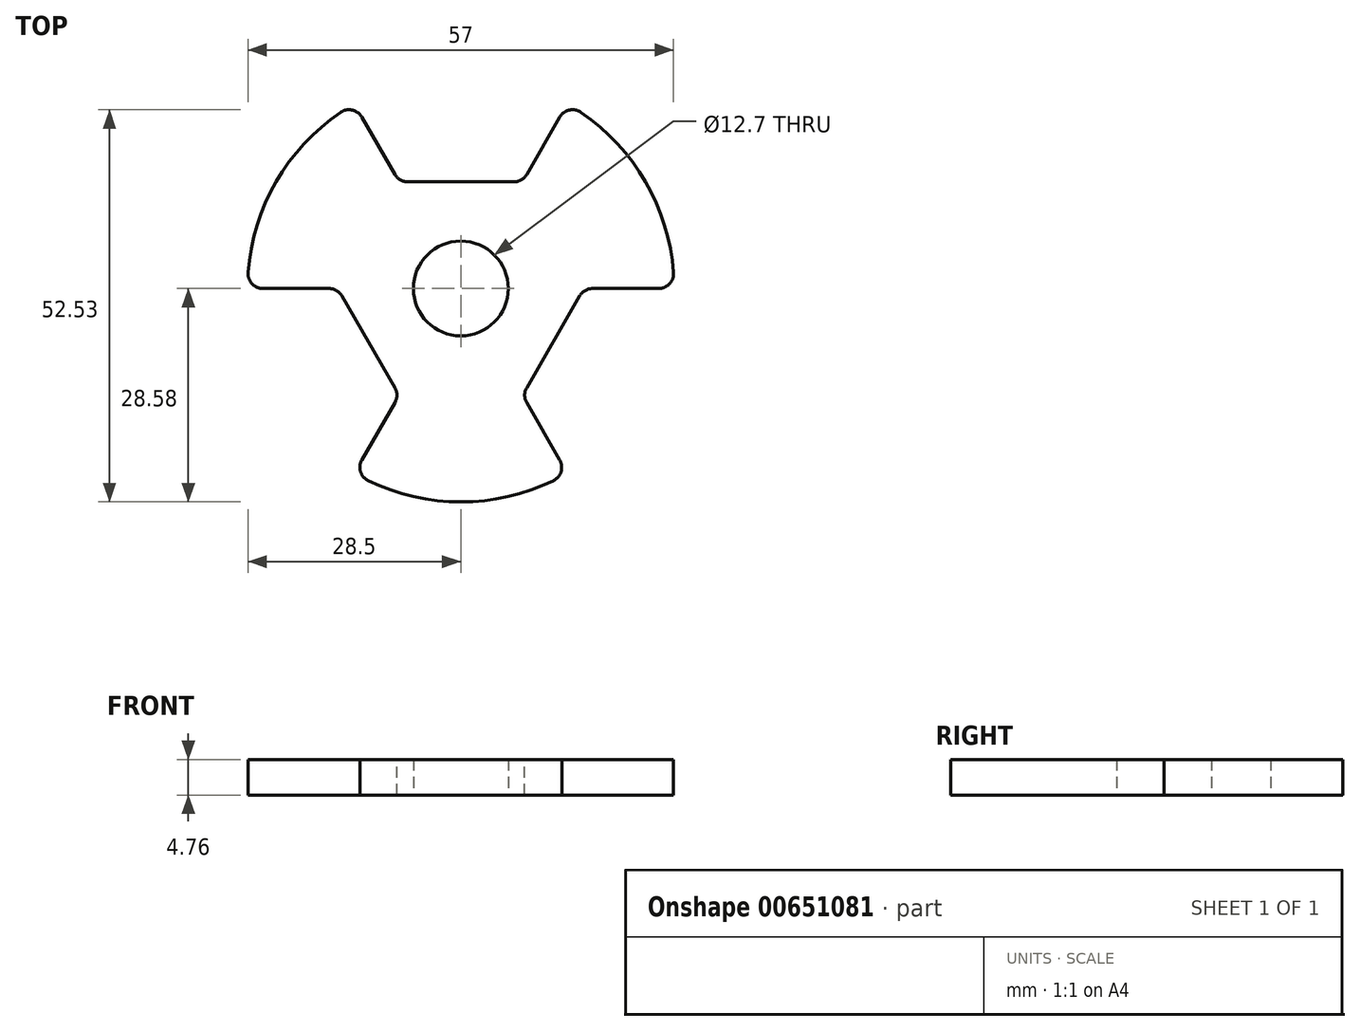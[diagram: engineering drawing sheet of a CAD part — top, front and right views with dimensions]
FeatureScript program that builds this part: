
annotation { "Feature Type Name" : "Feature", "Feature Type Description" : "" }
export const myFeature = defineFeature(function(context is Context, id is Id, definition is map)
    precondition{}
    {
        {
            var Q0;
            Q0=qCreatedBy(makeId("Top.planeOp"),FACE);
            var sketch = newSketch(context, id + "F0", { "sketchPlane" : qUnion([Q0])});
            skCircle(sketch, "E0", {"center": v(0, 0) * mm, "radius": 6.35 * mm});
            skCircle(sketch, "E1", {"center": v(0, 0) * mm, "radius": 28.58 * mm});
            skLineSegment(sketch, "E2", {"start": v(0, 0) * mm, "end": v(0, 28.58) * mm});
            skLineSegment(sketch, "E3", {"start": v(0, 0) * mm, "end": v(24.75, -14.29) * mm});
            skLineSegment(sketch, "E4", {"start": v(0, 0) * mm, "end": v(-24.75, -14.29) * mm});
            skLineSegment(sketch, "E5", {"start": v(0, 28.58) * mm, "end": v(-24.75, -14.29) * mm});
            skLineSegment(sketch, "E6", {"start": v(-24.75, -14.29) * mm, "end": v(24.75, -14.29) * mm});
            skLineSegment(sketch, "E7", {"start": v(24.75, -14.29) * mm, "end": v(0, 28.58) * mm});
            skLineSegment(sketch, "E8", {"start": v(0, 0) * mm, "end": v(0, -28.58) * mm});
            skPoint(sketch, "E8.endSnap0", {"position": v(0, -14.29) * mm});
            skLineSegment(sketch, "E9", {"start": v(0, 0) * mm, "end": v(24.75, 14.29) * mm});
            skLineSegment(sketch, "E10", {"start": v(0, 0) * mm, "end": v(-24.75, 14.29) * mm});
            skLineSegment(sketch, "E11", {"start": v(-24.75, 14.29) * mm, "end": v(0, -28.58) * mm});
            skLineSegment(sketch, "E12", {"start": v(24.75, 14.29) * mm, "end": v(0, -28.58) * mm});
            skLineSegment(sketch, "E13", {"start": v(-24.75, 14.29) * mm, "end": v(24.75, 14.29) * mm});
            skLineSegment(sketch, "E14", {"start": v(0, 0) * mm, "end": v(28.58, 0) * mm});
            skLineSegment(sketch, "E15", {"start": v(0, 0) * mm, "end": v(-14.29, -24.75) * mm});
            skLineSegment(sketch, "E16", {"start": v(0, 0) * mm, "end": v(-14.29, 24.75) * mm});
            skLineSegment(sketch, "E17", {"start": v(-14.29, 24.75) * mm, "end": v(-14.29, -24.75) * mm});
            skLineSegment(sketch, "E18", {"start": v(-14.29, -24.75) * mm, "end": v(28.58, 0) * mm});
            skLineSegment(sketch, "E19", {"start": v(28.58, 0) * mm, "end": v(-14.29, 24.75) * mm});
            skLineSegment(sketch, "E20", {"start": v(0, 0) * mm, "end": v(-28.58, 0) * mm});
            skLineSegment(sketch, "E21", {"start": v(0, 0) * mm, "end": v(14.29, -24.75) * mm});
            skLineSegment(sketch, "E22", {"start": v(0, 0) * mm, "end": v(14.29, 24.75) * mm});
            skLineSegment(sketch, "E23", {"start": v(14.29, 24.75) * mm, "end": v(-28.58, 0) * mm});
            skLineSegment(sketch, "E24", {"start": v(14.29, -24.75) * mm, "end": v(-28.58, 0) * mm});
            skLineSegment(sketch, "E25", {"start": v(14.29, 24.75) * mm, "end": v(14.29, -24.75) * mm});
            skCircle(sketch, "E26", {"center": v(0, 0) * mm, "radius": 5.08 * mm});
            skSolve(sketch);
        }
        {
            var Q0;
            {var subQ1=sQuery(id+"F0.wireOp",EDGE,"E0");var subQ7=sQuery(id+"F0.wireOp",EDGE,"E4");var subQ9=makeQuery(id+"F0.imprint","INTERSECT",VERTEX,{"derivedFrom":[subQ1,subQ7]});Q0=makeQuery(id+"F0.imprint","IMPRINT",FACE,{"disambiguationData":[TD([[makeQuery(id+"F0.imprint","IMPRINT",EDGE,{"disambiguationData":[TD([[subQ9,-1.0]])],"derivedFrom":subQ1}),-1.0]])]});}
            var Q1;
            {var subQ5=sQuery(id+"F0.wireOp",EDGE,"E0");var subQ7=sQuery(id+"F0.wireOp",EDGE,"E21");var subQ9=makeQuery(id+"F0.imprint","INTERSECT",VERTEX,{"derivedFrom":[subQ5,subQ7]});Q1=makeQuery(id+"F0.imprint","IMPRINT",FACE,{"disambiguationData":[TD([[makeQuery(id+"F0.imprint","IMPRINT",EDGE,{"disambiguationData":[TD([[subQ9,-1.0]])],"derivedFrom":subQ5}),-1.0]])]});}
            var Q2;
            {var subQ0=sQuery(id+"F0.wireOp",EDGE,"E14");var subQ1=sQuery(id+"F0.wireOp",EDGE,"E0");var subQ2=makeQuery(id+"F0.imprint","INTERSECT",VERTEX,{"derivedFrom":[subQ1,subQ0]});Q2=makeQuery(id+"F0.imprint","IMPRINT",FACE,{"disambiguationData":[TD([[makeQuery(id+"F0.imprint","IMPRINT",EDGE,{"disambiguationData":[TD([[subQ2,1.0]])],"derivedFrom":subQ1}),-1.0]])]});}
            var Q3;
            {var subQ3=sQuery(id+"F0.wireOp",EDGE,"E22");var subQ6=sQuery(id+"F0.wireOp",EDGE,"E0");var subQ9=makeQuery(id+"F0.imprint","INTERSECT",VERTEX,{"derivedFrom":[subQ6,subQ3]});Q3=makeQuery(id+"F0.imprint","IMPRINT",FACE,{"disambiguationData":[TD([[makeQuery(id+"F0.imprint","IMPRINT",EDGE,{"disambiguationData":[TD([[subQ9,-1.0]])],"derivedFrom":subQ6}),-1.0]])]});}
            var Q4;
            {var subQ1=sQuery(id+"F0.wireOp",EDGE,"E2");var subQ5=sQuery(id+"F0.wireOp",EDGE,"E0");var subQ6=makeQuery(id+"F0.imprint","INTERSECT",VERTEX,{"derivedFrom":[subQ5,subQ1]});Q4=makeQuery(id+"F0.imprint","IMPRINT",FACE,{"disambiguationData":[TD([[makeQuery(id+"F0.imprint","IMPRINT",EDGE,{"disambiguationData":[TD([[subQ6,-1.0]])],"derivedFrom":subQ5}),-1.0]])]});}
            var Q5;
            {var subQ3=sQuery(id+"F0.wireOp",EDGE,"E20");var subQ7=sQuery(id+"F0.wireOp",EDGE,"E0");var subQ9=makeQuery(id+"F0.imprint","INTERSECT",VERTEX,{"derivedFrom":[subQ7,subQ3]});Q5=makeQuery(id+"F0.imprint","IMPRINT",FACE,{"disambiguationData":[TD([[makeQuery(id+"F0.imprint","IMPRINT",EDGE,{"disambiguationData":[TD([[subQ9,-1.0]])],"derivedFrom":subQ7}),-1.0]])]});}
            var Q6;
            {var subQ0=sQuery(id+"F0.wireOp",EDGE,"E24");var subQ1=sQuery(id+"F0.wireOp",EDGE,"E11");var subQ2=makeQuery(id+"F0.imprint","INTERSECT",VERTEX,{"derivedFrom":[subQ1,subQ0]});Q6=makeQuery(id+"F0.imprint","IMPRINT",FACE,{"disambiguationData":[TD([[makeQuery(id+"F0.imprint","IMPRINT",EDGE,{"disambiguationData":[TD([[subQ2,1.0]])],"derivedFrom":subQ0}),1.0]])]});}
            var Q7;
            {var subQ0=sQuery(id+"F0.wireOp",EDGE,"E24");var subQ1=sQuery(id+"F0.wireOp",EDGE,"E6");var subQ2=makeQuery(id+"F0.imprint","INTERSECT",VERTEX,{"derivedFrom":[subQ1,subQ0]});Q7=makeQuery(id+"F0.imprint","IMPRINT",FACE,{"disambiguationData":[TD([[makeQuery(id+"F0.imprint","IMPRINT",EDGE,{"disambiguationData":[TD([[subQ2,-1.0]])],"derivedFrom":subQ0}),1.0]])]});}
            var Q8;
            {var subQ0=sQuery(id+"F0.wireOp",EDGE,"E24");var subQ1=sQuery(id+"F0.wireOp",EDGE,"E6");var subQ2=makeQuery(id+"F0.imprint","INTERSECT",VERTEX,{"derivedFrom":[subQ1,subQ0]});Q8=makeQuery(id+"F0.imprint","IMPRINT",FACE,{"disambiguationData":[TD([[makeQuery(id+"F0.imprint","IMPRINT",EDGE,{"disambiguationData":[TD([[subQ2,1.0]])],"derivedFrom":subQ1}),-1.0]])]});}
            var Q9;
            {var subQ0=sQuery(id+"F0.wireOp",EDGE,"E11");var subQ3=sQuery(id+"F0.wireOp",EDGE,"E18");var subQ5=makeQuery(id+"F0.imprint","INTERSECT",VERTEX,{"derivedFrom":[subQ0,subQ3]});Q9=makeQuery(id+"F0.imprint","IMPRINT",FACE,{"disambiguationData":[TD([[makeQuery(id+"F0.imprint","IMPRINT",EDGE,{"disambiguationData":[TD([[subQ5,-1.0]])],"derivedFrom":subQ3}),-1.0]])]});}
            var Q10;
            {var subQ0=sQuery(id+"F0.wireOp",EDGE,"E12");var subQ3=sQuery(id+"F0.wireOp",EDGE,"E24");var subQ5=makeQuery(id+"F0.imprint","INTERSECT",VERTEX,{"derivedFrom":[subQ0,subQ3]});Q10=makeQuery(id+"F0.imprint","IMPRINT",FACE,{"disambiguationData":[TD([[makeQuery(id+"F0.imprint","IMPRINT",EDGE,{"disambiguationData":[TD([[subQ5,-1.0]])],"derivedFrom":subQ3}),1.0]])]});}
            var Q11;
            {var subQ0=sQuery(id+"F0.wireOp",EDGE,"E18");var subQ1=sQuery(id+"F0.wireOp",EDGE,"E6");var subQ2=makeQuery(id+"F0.imprint","INTERSECT",VERTEX,{"derivedFrom":[subQ1,subQ0]});Q11=makeQuery(id+"F0.imprint","IMPRINT",FACE,{"disambiguationData":[TD([[makeQuery(id+"F0.imprint","IMPRINT",EDGE,{"disambiguationData":[TD([[subQ2,-1.0]])],"derivedFrom":subQ1}),-1.0]])]});}
            var Q12;
            {var subQ0=sQuery(id+"F0.wireOp",EDGE,"E18");var subQ1=sQuery(id+"F0.wireOp",EDGE,"E6");var subQ2=makeQuery(id+"F0.imprint","INTERSECT",VERTEX,{"derivedFrom":[subQ1,subQ0]});Q12=makeQuery(id+"F0.imprint","IMPRINT",FACE,{"disambiguationData":[TD([[makeQuery(id+"F0.imprint","IMPRINT",EDGE,{"disambiguationData":[TD([[subQ2,-1.0]])],"derivedFrom":subQ0}),-1.0]])]});}
            var Q13;
            {var subQ0=sQuery(id+"F0.wireOp",EDGE,"E18");var subQ1=sQuery(id+"F0.wireOp",EDGE,"E12");var subQ2=makeQuery(id+"F0.imprint","INTERSECT",VERTEX,{"derivedFrom":[subQ1,subQ0]});Q13=makeQuery(id+"F0.imprint","IMPRINT",FACE,{"disambiguationData":[TD([[makeQuery(id+"F0.imprint","IMPRINT",EDGE,{"disambiguationData":[TD([[subQ2,1.0]])],"derivedFrom":subQ0}),-1.0]])]});}
            var Q14;
            {var subQ0=sQuery(id+"F0.wireOp",EDGE,"E24");var subQ1=sQuery(id+"F0.wireOp",EDGE,"E6");var subQ2=makeQuery(id+"F0.imprint","INTERSECT",VERTEX,{"derivedFrom":[subQ1,subQ0]});Q14=makeQuery(id+"F0.imprint","IMPRINT",FACE,{"disambiguationData":[TD([[makeQuery(id+"F0.imprint","IMPRINT",EDGE,{"disambiguationData":[TD([[subQ2,-1.0]])],"derivedFrom":subQ1}),-1.0]])]});}
            var Q15;
            {var subQ0=sQuery(id+"F0.wireOp",EDGE,"E8");var subQ1=sQuery(id+"F0.wireOp",EDGE,"E6");var subQ2=makeQuery(id+"F0.imprint","INTERSECT",VERTEX,{"derivedFrom":[subQ1,subQ0]});Q15=makeQuery(id+"F0.imprint","IMPRINT",FACE,{"disambiguationData":[TD([[makeQuery(id+"F0.imprint","IMPRINT",EDGE,{"disambiguationData":[TD([[subQ2,-1.0]])],"derivedFrom":subQ1}),-1.0]])]});}
            var Q16;
            {var subQ0=sQuery(id+"F0.wireOp",EDGE,"E25");var subQ1=sQuery(id+"F0.wireOp",EDGE,"E12");var subQ2=makeQuery(id+"F0.imprint","INTERSECT",VERTEX,{"derivedFrom":[subQ1,subQ0]});Q16=makeQuery(id+"F0.imprint","IMPRINT",FACE,{"disambiguationData":[TD([[makeQuery(id+"F0.imprint","IMPRINT",EDGE,{"disambiguationData":[TD([[subQ2,1.0]])],"derivedFrom":subQ0}),1.0]])]});}
            var Q17;
            {var subQ0=sQuery(id+"F0.wireOp",EDGE,"E25");var subQ1=sQuery(id+"F0.wireOp",EDGE,"E7");var subQ2=makeQuery(id+"F0.imprint","INTERSECT",VERTEX,{"derivedFrom":[subQ1,subQ0]});Q17=makeQuery(id+"F0.imprint","IMPRINT",FACE,{"disambiguationData":[TD([[makeQuery(id+"F0.imprint","IMPRINT",EDGE,{"disambiguationData":[TD([[subQ2,1.0]])],"derivedFrom":subQ1}),-1.0]])]});}
            var Q18;
            {var subQ0=sQuery(id+"F0.wireOp",EDGE,"E25");var subQ1=sQuery(id+"F0.wireOp",EDGE,"E7");var subQ2=makeQuery(id+"F0.imprint","INTERSECT",VERTEX,{"derivedFrom":[subQ1,subQ0]});Q18=makeQuery(id+"F0.imprint","IMPRINT",FACE,{"disambiguationData":[TD([[makeQuery(id+"F0.imprint","IMPRINT",EDGE,{"disambiguationData":[TD([[subQ2,-1.0]])],"derivedFrom":subQ0}),1.0]])]});}
            var Q19;
            {var subQ0=sQuery(id+"F0.wireOp",EDGE,"E25");var subQ1=sQuery(id+"F0.wireOp",EDGE,"E7");var subQ2=makeQuery(id+"F0.imprint","INTERSECT",VERTEX,{"derivedFrom":[subQ1,subQ0]});Q19=makeQuery(id+"F0.imprint","IMPRINT",FACE,{"disambiguationData":[TD([[makeQuery(id+"F0.imprint","IMPRINT",EDGE,{"disambiguationData":[TD([[subQ2,-1.0]])],"derivedFrom":subQ1}),-1.0]])]});}
            var Q20;
            {var subQ0=sQuery(id+"F0.wireOp",EDGE,"E9");var subQ1=sQuery(id+"F0.wireOp",EDGE,"E7");var subQ2=makeQuery(id+"F0.imprint","INTERSECT",VERTEX,{"derivedFrom":[subQ1,subQ0]});Q20=makeQuery(id+"F0.imprint","IMPRINT",FACE,{"disambiguationData":[TD([[makeQuery(id+"F0.imprint","IMPRINT",EDGE,{"disambiguationData":[TD([[subQ2,-1.0]])],"derivedFrom":subQ1}),-1.0]])]});}
            var Q21;
            {var subQ0=sQuery(id+"F0.wireOp",EDGE,"E19");var subQ1=sQuery(id+"F0.wireOp",EDGE,"E7");var subQ2=makeQuery(id+"F0.imprint","INTERSECT",VERTEX,{"derivedFrom":[subQ1,subQ0]});Q21=makeQuery(id+"F0.imprint","IMPRINT",FACE,{"disambiguationData":[TD([[makeQuery(id+"F0.imprint","IMPRINT",EDGE,{"disambiguationData":[TD([[subQ2,-1.0]])],"derivedFrom":subQ1}),-1.0]])]});}
            var Q22;
            {var subQ0=sQuery(id+"F0.wireOp",EDGE,"E19");var subQ1=sQuery(id+"F0.wireOp",EDGE,"E13");var subQ2=makeQuery(id+"F0.imprint","INTERSECT",VERTEX,{"derivedFrom":[subQ1,subQ0]});Q22=makeQuery(id+"F0.imprint","IMPRINT",FACE,{"disambiguationData":[TD([[makeQuery(id+"F0.imprint","IMPRINT",EDGE,{"disambiguationData":[TD([[subQ2,1.0]])],"derivedFrom":subQ0}),-1.0]])]});}
            var Q23;
            {var subQ0=sQuery(id+"F0.wireOp",EDGE,"E19");var subQ1=sQuery(id+"F0.wireOp",EDGE,"E7");var subQ2=makeQuery(id+"F0.imprint","INTERSECT",VERTEX,{"derivedFrom":[subQ1,subQ0]});Q23=makeQuery(id+"F0.imprint","IMPRINT",FACE,{"disambiguationData":[TD([[makeQuery(id+"F0.imprint","IMPRINT",EDGE,{"disambiguationData":[TD([[subQ2,-1.0]])],"derivedFrom":subQ0}),-1.0]])]});}
            var Q24;
            {var subQ0=sQuery(id+"F0.wireOp",EDGE,"E13");var subQ3=sQuery(id+"F0.wireOp",EDGE,"E25");var subQ5=makeQuery(id+"F0.imprint","INTERSECT",VERTEX,{"derivedFrom":[subQ0,subQ3]});Q24=makeQuery(id+"F0.imprint","IMPRINT",FACE,{"disambiguationData":[TD([[makeQuery(id+"F0.imprint","IMPRINT",EDGE,{"disambiguationData":[TD([[subQ5,-1.0]])],"derivedFrom":subQ3}),1.0]])]});}
            var Q25;
            {var subQ0=sQuery(id+"F0.wireOp",EDGE,"E12");var subQ3=sQuery(id+"F0.wireOp",EDGE,"E19");var subQ5=makeQuery(id+"F0.imprint","INTERSECT",VERTEX,{"derivedFrom":[subQ0,subQ3]});Q25=makeQuery(id+"F0.imprint","IMPRINT",FACE,{"disambiguationData":[TD([[makeQuery(id+"F0.imprint","IMPRINT",EDGE,{"disambiguationData":[TD([[subQ5,-1.0]])],"derivedFrom":subQ3}),-1.0]])]});}
            var Q26;
            {var subQ0=sQuery(id+"F0.wireOp",EDGE,"E17");var subQ1=sQuery(id+"F0.wireOp",EDGE,"E11");var subQ2=makeQuery(id+"F0.imprint","INTERSECT",VERTEX,{"derivedFrom":[subQ1,subQ0]});Q26=makeQuery(id+"F0.imprint","IMPRINT",FACE,{"disambiguationData":[TD([[makeQuery(id+"F0.imprint","IMPRINT",EDGE,{"disambiguationData":[TD([[subQ2,1.0]])],"derivedFrom":subQ0}),-1.0]])]});}
            var Q27;
            {var subQ0=sQuery(id+"F0.wireOp",EDGE,"E17");var subQ1=sQuery(id+"F0.wireOp",EDGE,"E5");var subQ2=makeQuery(id+"F0.imprint","INTERSECT",VERTEX,{"derivedFrom":[subQ1,subQ0]});Q27=makeQuery(id+"F0.imprint","IMPRINT",FACE,{"disambiguationData":[TD([[makeQuery(id+"F0.imprint","IMPRINT",EDGE,{"disambiguationData":[TD([[subQ2,-1.0]])],"derivedFrom":subQ0}),-1.0]])]});}
            var Q28;
            {var subQ0=sQuery(id+"F0.wireOp",EDGE,"E17");var subQ1=sQuery(id+"F0.wireOp",EDGE,"E5");var subQ2=makeQuery(id+"F0.imprint","INTERSECT",VERTEX,{"derivedFrom":[subQ1,subQ0]});Q28=makeQuery(id+"F0.imprint","IMPRINT",FACE,{"disambiguationData":[TD([[makeQuery(id+"F0.imprint","IMPRINT",EDGE,{"disambiguationData":[TD([[subQ2,-1.0]])],"derivedFrom":subQ1}),-1.0]])]});}
            var Q29;
            {var subQ0=sQuery(id+"F0.wireOp",EDGE,"E10");var subQ1=sQuery(id+"F0.wireOp",EDGE,"E5");var subQ2=makeQuery(id+"F0.imprint","INTERSECT",VERTEX,{"derivedFrom":[subQ1,subQ0]});Q29=makeQuery(id+"F0.imprint","IMPRINT",FACE,{"disambiguationData":[TD([[makeQuery(id+"F0.imprint","IMPRINT",EDGE,{"disambiguationData":[TD([[subQ2,-1.0]])],"derivedFrom":subQ1}),-1.0]])]});}
            var Q30;
            {var subQ0=sQuery(id+"F0.wireOp",EDGE,"E23");var subQ1=sQuery(id+"F0.wireOp",EDGE,"E5");var subQ2=makeQuery(id+"F0.imprint","INTERSECT",VERTEX,{"derivedFrom":[subQ1,subQ0]});Q30=makeQuery(id+"F0.imprint","IMPRINT",FACE,{"disambiguationData":[TD([[makeQuery(id+"F0.imprint","IMPRINT",EDGE,{"disambiguationData":[TD([[subQ2,1.0]])],"derivedFrom":subQ0}),-1.0]])]});}
            var Q31;
            {var subQ0=sQuery(id+"F0.wireOp",EDGE,"E23");var subQ1=sQuery(id+"F0.wireOp",EDGE,"E13");var subQ2=makeQuery(id+"F0.imprint","INTERSECT",VERTEX,{"derivedFrom":[subQ1,subQ0]});Q31=makeQuery(id+"F0.imprint","IMPRINT",FACE,{"disambiguationData":[TD([[makeQuery(id+"F0.imprint","IMPRINT",EDGE,{"disambiguationData":[TD([[subQ2,-1.0]])],"derivedFrom":subQ0}),-1.0]])]});}
            var Q32;
            {var subQ0=sQuery(id+"F0.wireOp",EDGE,"E23");var subQ1=sQuery(id+"F0.wireOp",EDGE,"E5");var subQ2=makeQuery(id+"F0.imprint","INTERSECT",VERTEX,{"derivedFrom":[subQ1,subQ0]});Q32=makeQuery(id+"F0.imprint","IMPRINT",FACE,{"disambiguationData":[TD([[makeQuery(id+"F0.imprint","IMPRINT",EDGE,{"disambiguationData":[TD([[subQ2,-1.0]])],"derivedFrom":subQ1}),-1.0]])]});}
            var Q33;
            {var subQ0=sQuery(id+"F0.wireOp",EDGE,"E23");var subQ1=sQuery(id+"F0.wireOp",EDGE,"E5");var subQ2=makeQuery(id+"F0.imprint","INTERSECT",VERTEX,{"derivedFrom":[subQ1,subQ0]});Q33=makeQuery(id+"F0.imprint","IMPRINT",FACE,{"disambiguationData":[TD([[makeQuery(id+"F0.imprint","IMPRINT",EDGE,{"disambiguationData":[TD([[subQ2,1.0]])],"derivedFrom":subQ1}),-1.0]])]});}
            var Q34;
            {var subQ0=sQuery(id+"F0.wireOp",EDGE,"E13");var subQ3=sQuery(id+"F0.wireOp",EDGE,"E17");var subQ5=makeQuery(id+"F0.imprint","INTERSECT",VERTEX,{"derivedFrom":[subQ0,subQ3]});Q34=makeQuery(id+"F0.imprint","IMPRINT",FACE,{"disambiguationData":[TD([[makeQuery(id+"F0.imprint","IMPRINT",EDGE,{"disambiguationData":[TD([[subQ5,-1.0]])],"derivedFrom":subQ3}),-1.0]])]});}
            var Q35;
            {var subQ0=sQuery(id+"F0.wireOp",EDGE,"E11");var subQ3=sQuery(id+"F0.wireOp",EDGE,"E23");var subQ5=makeQuery(id+"F0.imprint","INTERSECT",VERTEX,{"derivedFrom":[subQ0,subQ3]});Q35=makeQuery(id+"F0.imprint","IMPRINT",FACE,{"disambiguationData":[TD([[makeQuery(id+"F0.imprint","IMPRINT",EDGE,{"disambiguationData":[TD([[subQ5,1.0]])],"derivedFrom":subQ3}),-1.0]])]});}
            var Q36;
            {var subQ0=sQuery(id+"F0.wireOp",EDGE,"E11");var subQ3=sQuery(id+"F0.wireOp",EDGE,"E23");var subQ5=makeQuery(id+"F0.imprint","INTERSECT",VERTEX,{"derivedFrom":[subQ0,subQ3]});Q36=makeQuery(id+"F0.imprint","IMPRINT",FACE,{"disambiguationData":[TD([[makeQuery(id+"F0.imprint","IMPRINT",EDGE,{"disambiguationData":[TD([[subQ5,1.0]])],"derivedFrom":subQ0}),-1.0]])]});}
            var Q37;
            {var subQ0=sQuery(id+"F0.wireOp",EDGE,"E13");var subQ3=sQuery(id+"F0.wireOp",EDGE,"E17");var subQ5=makeQuery(id+"F0.imprint","INTERSECT",VERTEX,{"derivedFrom":[subQ0,subQ3]});Q37=makeQuery(id+"F0.imprint","IMPRINT",FACE,{"disambiguationData":[TD([[makeQuery(id+"F0.imprint","IMPRINT",EDGE,{"disambiguationData":[TD([[subQ5,1.0]])],"derivedFrom":subQ0}),1.0]])]});}
            var Q38;
            {var subQ0=sQuery(id+"F0.wireOp",EDGE,"E11");var subQ3=sQuery(id+"F0.wireOp",EDGE,"E18");var subQ5=makeQuery(id+"F0.imprint","INTERSECT",VERTEX,{"derivedFrom":[subQ0,subQ3]});Q38=makeQuery(id+"F0.imprint","IMPRINT",FACE,{"disambiguationData":[TD([[makeQuery(id+"F0.imprint","IMPRINT",EDGE,{"disambiguationData":[TD([[subQ5,-1.0]])],"derivedFrom":subQ0}),-1.0]])]});}
            var Q39;
            {var subQ0=sQuery(id+"F0.wireOp",EDGE,"E12");var subQ3=sQuery(id+"F0.wireOp",EDGE,"E24");var subQ5=makeQuery(id+"F0.imprint","INTERSECT",VERTEX,{"derivedFrom":[subQ0,subQ3]});Q39=makeQuery(id+"F0.imprint","IMPRINT",FACE,{"disambiguationData":[TD([[makeQuery(id+"F0.imprint","IMPRINT",EDGE,{"disambiguationData":[TD([[subQ5,-1.0]])],"derivedFrom":subQ0}),1.0]])]});}
            var Q40;
            {var subQ0=sQuery(id+"F0.wireOp",EDGE,"E13");var subQ3=sQuery(id+"F0.wireOp",EDGE,"E25");var subQ5=makeQuery(id+"F0.imprint","INTERSECT",VERTEX,{"derivedFrom":[subQ0,subQ3]});Q40=makeQuery(id+"F0.imprint","IMPRINT",FACE,{"disambiguationData":[TD([[makeQuery(id+"F0.imprint","IMPRINT",EDGE,{"disambiguationData":[TD([[subQ5,-1.0]])],"derivedFrom":subQ0}),1.0]])]});}
            var Q41;
            {var subQ0=sQuery(id+"F0.wireOp",EDGE,"E12");var subQ3=sQuery(id+"F0.wireOp",EDGE,"E19");var subQ5=makeQuery(id+"F0.imprint","INTERSECT",VERTEX,{"derivedFrom":[subQ0,subQ3]});Q41=makeQuery(id+"F0.imprint","IMPRINT",FACE,{"disambiguationData":[TD([[makeQuery(id+"F0.imprint","IMPRINT",EDGE,{"disambiguationData":[TD([[subQ5,1.0]])],"derivedFrom":subQ0}),1.0]])]});}
            var Q42;
            {var subQ0=sQuery(id+"F0.wireOp",EDGE,"E19");var subQ1=sQuery(id+"F0.wireOp",EDGE,"E12");var subQ2=makeQuery(id+"F0.imprint","INTERSECT",VERTEX,{"derivedFrom":[subQ1,subQ0]});Q42=makeQuery(id+"F0.imprint","IMPRINT",FACE,{"disambiguationData":[TD([[makeQuery(id+"F0.imprint","IMPRINT",EDGE,{"disambiguationData":[TD([[subQ2,-1.0]])],"derivedFrom":subQ1}),1.0]])]});}
            var Q43;
            {var subQ0=sQuery(id+"F0.wireOp",EDGE,"E25");var subQ1=sQuery(id+"F0.wireOp",EDGE,"E13");var subQ2=makeQuery(id+"F0.imprint","INTERSECT",VERTEX,{"derivedFrom":[subQ1,subQ0]});Q43=makeQuery(id+"F0.imprint","IMPRINT",FACE,{"disambiguationData":[TD([[makeQuery(id+"F0.imprint","IMPRINT",EDGE,{"disambiguationData":[TD([[subQ2,1.0]])],"derivedFrom":subQ1}),1.0]])]});}
            var Q44;
            {var subQ0=sQuery(id+"F0.wireOp",EDGE,"E24");var subQ1=sQuery(id+"F0.wireOp",EDGE,"E12");var subQ2=makeQuery(id+"F0.imprint","INTERSECT",VERTEX,{"derivedFrom":[subQ1,subQ0]});Q44=makeQuery(id+"F0.imprint","IMPRINT",FACE,{"disambiguationData":[TD([[makeQuery(id+"F0.imprint","IMPRINT",EDGE,{"disambiguationData":[TD([[subQ2,1.0]])],"derivedFrom":subQ1}),1.0]])]});}
            var Q45;
            {var subQ0=sQuery(id+"F0.wireOp",EDGE,"E18");var subQ1=sQuery(id+"F0.wireOp",EDGE,"E11");var subQ2=makeQuery(id+"F0.imprint","INTERSECT",VERTEX,{"derivedFrom":[subQ1,subQ0]});Q45=makeQuery(id+"F0.imprint","IMPRINT",FACE,{"disambiguationData":[TD([[makeQuery(id+"F0.imprint","IMPRINT",EDGE,{"disambiguationData":[TD([[subQ2,1.0]])],"derivedFrom":subQ1}),-1.0]])]});}
            var Q46;
            {var subQ0=sQuery(id+"F0.wireOp",EDGE,"E23");var subQ1=sQuery(id+"F0.wireOp",EDGE,"E11");var subQ2=makeQuery(id+"F0.imprint","INTERSECT",VERTEX,{"derivedFrom":[subQ1,subQ0]});Q46=makeQuery(id+"F0.imprint","IMPRINT",FACE,{"disambiguationData":[TD([[makeQuery(id+"F0.imprint","IMPRINT",EDGE,{"disambiguationData":[TD([[subQ2,-1.0]])],"derivedFrom":subQ1}),-1.0]])]});}
            var Q47;
            {var subQ0=sQuery(id+"F0.wireOp",EDGE,"E17");var subQ1=sQuery(id+"F0.wireOp",EDGE,"E13");var subQ2=makeQuery(id+"F0.imprint","INTERSECT",VERTEX,{"derivedFrom":[subQ1,subQ0]});Q47=makeQuery(id+"F0.imprint","IMPRINT",FACE,{"disambiguationData":[TD([[makeQuery(id+"F0.imprint","IMPRINT",EDGE,{"disambiguationData":[TD([[subQ2,-1.0]])],"derivedFrom":subQ1}),1.0]])]});}
            var Q48;
            {var subQ0=sQuery(id+"F0.wireOp",EDGE,"E9");var subQ1=sQuery(id+"F0.wireOp",EDGE,"E0");var subQ2=makeQuery(id+"F0.imprint","INTERSECT",VERTEX,{"derivedFrom":[subQ1,subQ0]});Q48=makeQuery(id+"F0.imprint","IMPRINT",FACE,{"disambiguationData":[TD([[makeQuery(id+"F0.imprint","IMPRINT",EDGE,{"disambiguationData":[TD([[subQ2,-1.0]])],"derivedFrom":subQ1}),-1.0]])]});}
            var Q49;
            {var subQ1=sQuery(id+"F0.wireOp",EDGE,"E0");var subQ7=sQuery(id+"F0.wireOp",EDGE,"E9");var subQ9=makeQuery(id+"F0.imprint","INTERSECT",VERTEX,{"derivedFrom":[subQ1,subQ7]});Q49=makeQuery(id+"F0.imprint","IMPRINT",FACE,{"disambiguationData":[TD([[makeQuery(id+"F0.imprint","IMPRINT",EDGE,{"disambiguationData":[TD([[subQ9,1.0]])],"derivedFrom":subQ1}),-1.0]])]});}
            var Q50;
            {var subQ0=sQuery(id+"F0.wireOp",EDGE,"E10");var subQ7=sQuery(id+"F0.wireOp",EDGE,"E0");var subQ8=makeQuery(id+"F0.imprint","INTERSECT",VERTEX,{"derivedFrom":[subQ7,subQ0]});Q50=makeQuery(id+"F0.imprint","IMPRINT",FACE,{"disambiguationData":[TD([[makeQuery(id+"F0.imprint","IMPRINT",EDGE,{"disambiguationData":[TD([[subQ8,-1.0]])],"derivedFrom":subQ7}),-1.0]])]});}
            var Q51;
            {var subQ1=sQuery(id+"F0.wireOp",EDGE,"E0");var subQ7=sQuery(id+"F0.wireOp",EDGE,"E16");var subQ8=makeQuery(id+"F0.imprint","INTERSECT",VERTEX,{"derivedFrom":[subQ1,subQ7]});Q51=makeQuery(id+"F0.imprint","IMPRINT",FACE,{"disambiguationData":[TD([[makeQuery(id+"F0.imprint","IMPRINT",EDGE,{"disambiguationData":[TD([[subQ8,-1.0]])],"derivedFrom":subQ1}),-1.0]])]});}
            var Q52;
            {var subQ0=sQuery(id+"F0.wireOp",EDGE,"E15");var subQ1=sQuery(id+"F0.wireOp",EDGE,"E0");var subQ2=makeQuery(id+"F0.imprint","INTERSECT",VERTEX,{"derivedFrom":[subQ1,subQ0]});Q52=makeQuery(id+"F0.imprint","IMPRINT",FACE,{"disambiguationData":[TD([[makeQuery(id+"F0.imprint","IMPRINT",EDGE,{"disambiguationData":[TD([[subQ2,-1.0]])],"derivedFrom":subQ1}),-1.0]])]});}
            var Q53;
            {var subQ5=sQuery(id+"F0.wireOp",EDGE,"E8");var subQ7=sQuery(id+"F0.wireOp",EDGE,"E0");var subQ8=makeQuery(id+"F0.imprint","INTERSECT",VERTEX,{"derivedFrom":[subQ7,subQ5]});Q53=makeQuery(id+"F0.imprint","IMPRINT",FACE,{"disambiguationData":[TD([[makeQuery(id+"F0.imprint","IMPRINT",EDGE,{"disambiguationData":[TD([[subQ8,-1.0]])],"derivedFrom":subQ7}),-1.0]])]});}
            extrude(context, id + "F1", {"entities" : qUnion([Q0, Q1, Q2, Q3, Q4, Q5, Q6, Q7, Q8, Q9, Q10, Q11, Q12, Q13, Q14, Q15, Q16, Q17, Q18, Q19, Q20, Q21, Q22, Q23, Q24, Q25, Q26, Q27, Q28, Q29, Q30, Q31, Q32, Q33, Q34, Q35, Q36, Q37, Q38, Q39, Q40, Q41, Q42, Q43, Q44, Q45, Q46, Q47, Q48, Q49, Q50, Q51, Q52, Q53]), "depth" : 4.76 * mm, "offsetDistance" : 25.4 * mm});
        }
        {
            var Q0;
            Q0=makeQuery(id+"F1.opExtrude","SWEPT_EDGE",EDGE,{"disambiguationData":[OSD([sQuery(id+"F0.wireOp",EDGE,"E1"),sQuery(id+"F0.wireOp",EDGE,"E20"),sQuery(id+"F0.wireOp",EDGE,"E23"),sQuery(id+"F0.wireOp",EDGE,"E24")])]});
            var Q1;
            Q1=makeQuery(id+"F1.opExtrude","SWEPT_EDGE",EDGE,{"disambiguationData":[OSD([sQuery(id+"F0.wireOp",EDGE,"E1"),sQuery(id+"F0.wireOp",EDGE,"E14"),sQuery(id+"F0.wireOp",EDGE,"E18"),sQuery(id+"F0.wireOp",EDGE,"E19")])]});
            var Q2;
            Q2=makeQuery(id+"F1.opExtrude","SWEPT_EDGE",EDGE,{"disambiguationData":[OSD([sQuery(id+"F0.wireOp",EDGE,"E1"),sQuery(id+"F0.wireOp",EDGE,"E21"),sQuery(id+"F0.wireOp",EDGE,"E24"),sQuery(id+"F0.wireOp",EDGE,"E25")])]});
            var Q3;
            Q3=makeQuery(id+"F1.opExtrude","SWEPT_EDGE",EDGE,{"disambiguationData":[OSD([sQuery(id+"F0.wireOp",EDGE,"E1"),sQuery(id+"F0.wireOp",EDGE,"E15"),sQuery(id+"F0.wireOp",EDGE,"E17"),sQuery(id+"F0.wireOp",EDGE,"E18")])]});
            var Q4;
            Q4=makeQuery(id+"F1.opExtrude","SWEPT_EDGE",EDGE,{"disambiguationData":[OSD([sQuery(id+"F0.wireOp",EDGE,"E1"),sQuery(id+"F0.wireOp",EDGE,"E16"),sQuery(id+"F0.wireOp",EDGE,"E17"),sQuery(id+"F0.wireOp",EDGE,"E19")])]});
            var Q5;
            Q5=makeQuery(id+"F1.opExtrude","SWEPT_EDGE",EDGE,{"disambiguationData":[OSD([sQuery(id+"F0.wireOp",EDGE,"E1"),sQuery(id+"F0.wireOp",EDGE,"E22"),sQuery(id+"F0.wireOp",EDGE,"E23"),sQuery(id+"F0.wireOp",EDGE,"E25")])]});
            var Q6;
            Q6=makeQuery(id+"F1.opExtrude","SWEPT_EDGE",EDGE,{"disambiguationData":[OSD([sQuery(id+"F0.wireOp",EDGE,"E6"),sQuery(id+"F0.wireOp",EDGE,"E12"),sQuery(id+"F0.wireOp",EDGE,"E21")])]});
            var Q7;
            Q7=makeQuery(id+"F1.opExtrude","SWEPT_EDGE",EDGE,{"disambiguationData":[OSD([sQuery(id+"F0.wireOp",EDGE,"E5"),sQuery(id+"F0.wireOp",EDGE,"E13"),sQuery(id+"F0.wireOp",EDGE,"E16")])]});
            var Q8;
            Q8=makeQuery(id+"F1.opExtrude","SWEPT_EDGE",EDGE,{"disambiguationData":[OSD([sQuery(id+"F0.wireOp",EDGE,"E7"),sQuery(id+"F0.wireOp",EDGE,"E13"),sQuery(id+"F0.wireOp",EDGE,"E22")])]});
            var Q9;
            Q9=makeQuery(id+"F1.opExtrude","SWEPT_EDGE",EDGE,{"disambiguationData":[OSD([sQuery(id+"F0.wireOp",EDGE,"E5"),sQuery(id+"F0.wireOp",EDGE,"E11"),sQuery(id+"F0.wireOp",EDGE,"E20")])]});
            var Q10;
            Q10=makeQuery(id+"F1.opExtrude","SWEPT_EDGE",EDGE,{"disambiguationData":[OSD([sQuery(id+"F0.wireOp",EDGE,"E6"),sQuery(id+"F0.wireOp",EDGE,"E11"),sQuery(id+"F0.wireOp",EDGE,"E15")])]});
            var Q11;
            Q11=makeQuery(id+"F1.opExtrude","SWEPT_EDGE",EDGE,{"disambiguationData":[OSD([sQuery(id+"F0.wireOp",EDGE,"E7"),sQuery(id+"F0.wireOp",EDGE,"E12"),sQuery(id+"F0.wireOp",EDGE,"E14")])]});
            fillet(context, id + "F2", {"entities" : qUnion([Q0, Q1, Q2, Q3, Q4, Q5, Q6, Q7, Q8, Q9, Q10, Q11]), "radius" : 2 * mm, "tangentPropagation" : true, "allowEdgeOverflow" : false});
        }
    });
